# Revit family: BM-00006_CT705ELN_G
name_source: partatom
category: Plumbing Fixtures
revit_build: Autodesk Revit LT 2015 (Build: 20140606_1530(x64)
units: mm (PartAtom-declared; Revit-internal decimal feet)

## types (1)
- BM-00006_CT705ELN_G
    Codes/Standards = • Meets and exceeds ASME A112.19.2/CSA B45.1, ASME A112.19.14,
• Certifications: IAPMO(cUPC), State of Massachusetts , City of Los Angeles, and others
• Code compliance: UPC, IPC, NSPC, NPC Canada, and others
• ADA compliant
    Colors/Finishes = Standard #01 Cotton
    Manufacturer = TOTO USA
    Model = CT705ELN(G)
    Specifications = • Water Use 1.28GPF/4.8LPF
(or 1.6GPF/6.0LPF when used with 1.6GPF flush valve)
• Flush System Siphon jet flushing action
• Min. Water Pressure 35 psi (flowing)
• Min. Flow Rate 23 GPM
• Water Surface 10-3/4" x 9-1/4"
• Trap Diameter 1-7/8"
• Rough-in 12", or 10"
• Trap Seal 2-3/8"
• Warranty One Year Limited Warranty
• Material Vitreous china
• Shipping Weight CT705ELN(G) - 56.5lbs
• Shipping Dimensions CT705ELN(G)
26-1/2"L x 9-1/2" W1 x 16-1/4"W2 x 19-1/2"H
    Type Comments = Shown with SC134 & TET1LA#32

## geometry (parser evidence)
native form markers: Sweep x14
no freeform markers — native parametric forms only
